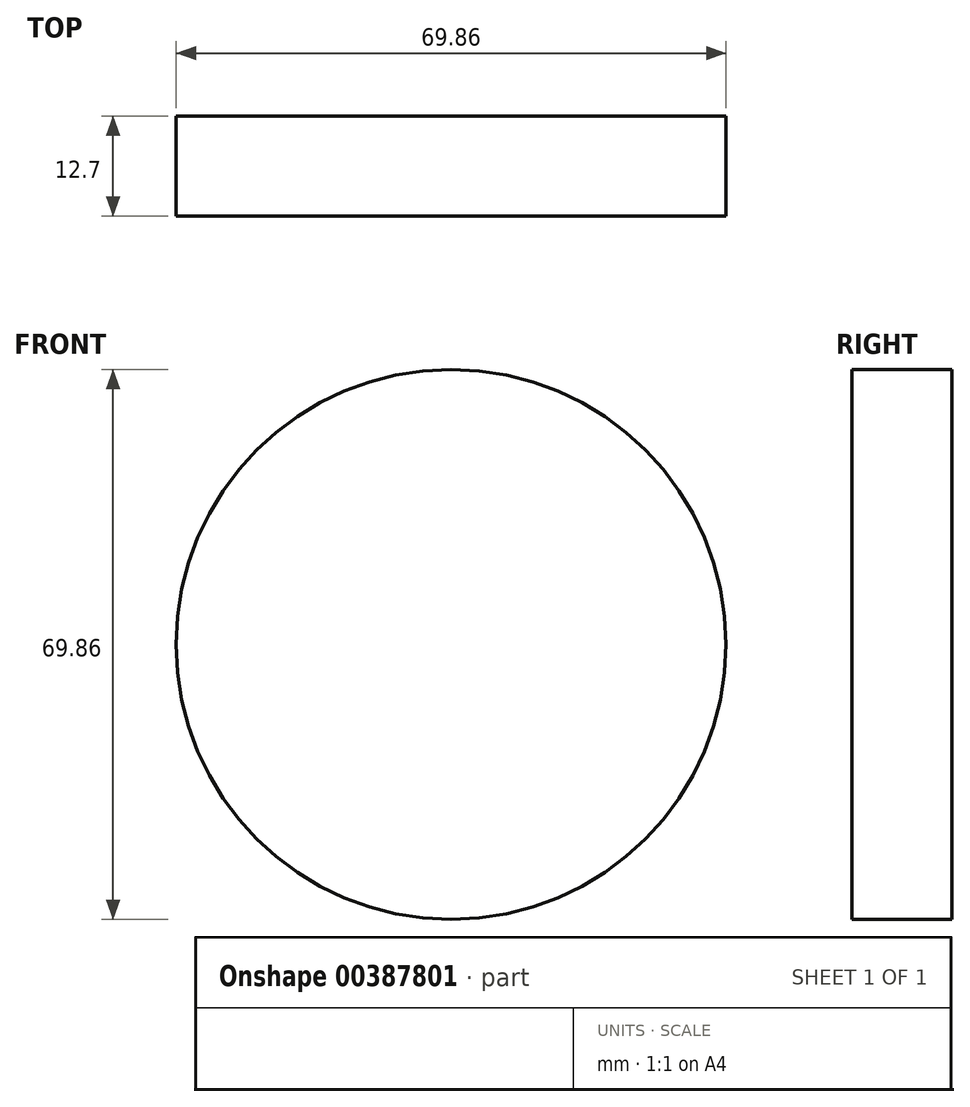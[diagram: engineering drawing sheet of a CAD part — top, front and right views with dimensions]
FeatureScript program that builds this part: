
annotation { "Feature Type Name" : "Feature", "Feature Type Description" : "" }
export const myFeature = defineFeature(function(context is Context, id is Id, definition is map)
    precondition{}
    {
        {
            var Q0;
            Q0=qCreatedBy(makeId("Front.planeOp"),FACE);
            var sketch = newSketch(context, id + "F0", { "sketchPlane" : qUnion([Q0])});
            skCircle(sketch, "E0", {"center": v(0, 0) * mm, "radius": 34.93 * mm});
            skCircle(sketch, "E1", {"center": v(47.55, 8) * mm, "radius": 13.29 * mm});
            skSolve(sketch);
        }
        {
            var Q0;
            Q0=makeQuery(id+"F0.imprint","IMPRINT",FACE,{"disambiguationData":[TD([[makeQuery(id+"F0.imprint","IMPRINT",EDGE,{"derivedFrom":sQuery(id+"F0.wireOp",EDGE,"E0")}),1.0]])]});
            extrude(context, id + "F1", {"entities" : qUnion([Q0]), "depth" : 12.7 * mm});
        }
    });
